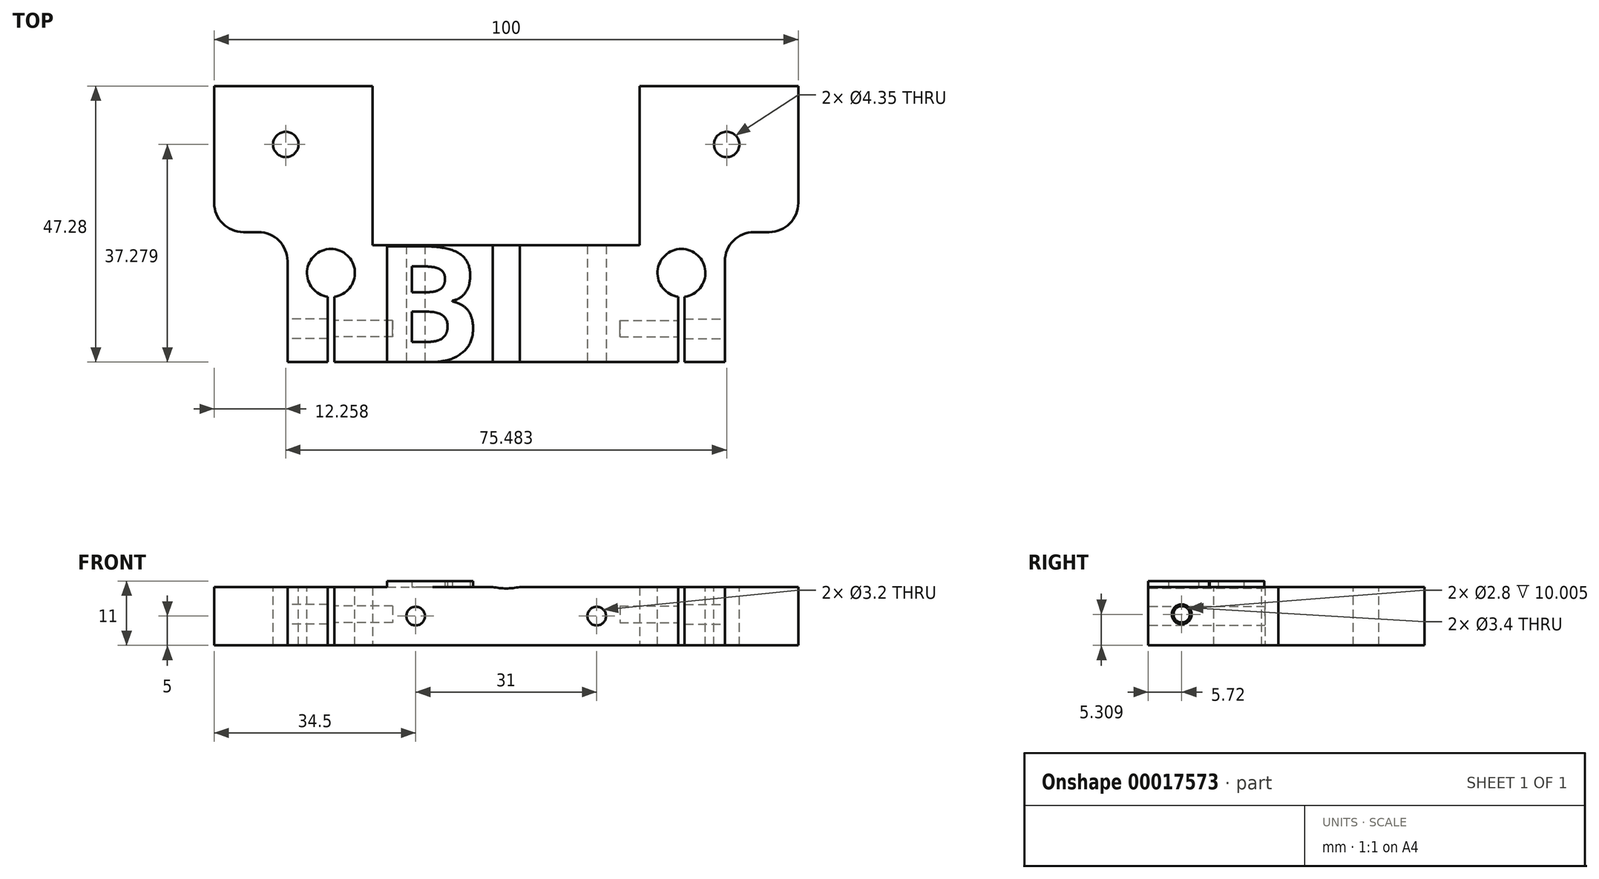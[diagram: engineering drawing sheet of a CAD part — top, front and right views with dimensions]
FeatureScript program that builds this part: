
annotation { "Feature Type Name" : "Feature", "Feature Type Description" : "" }
export const myFeature = defineFeature(function(context is Context, id is Id, definition is map)
    precondition{}
    {
        {
            var Q0;
            Q0=qCreatedBy(makeId("Top.planeOp"),FACE);
            var sketch = newSketch(context, id + "F0", { "sketchPlane" : qUnion([Q0])});
            skLineSegment(sketch, "E0", {"start": v(0, -13.82) * mm, "end": v(-37.44, -13.82) * mm});
            skLineSegment(sketch, "E1", {"start": v(-37.44, -13.82) * mm, "end": v(-37.44, 8.46) * mm});
            skLineSegment(sketch, "E2", {"start": v(-37.44, 8.46) * mm, "end": v(-50, 8.46) * mm});
            skLineSegment(sketch, "E3", {"start": v(-50, 8.46) * mm, "end": v(-50, 33.46) * mm});
            skLineSegment(sketch, "E4", {"start": v(-50, 33.46) * mm, "end": v(-22.87, 33.46) * mm});
            skLineSegment(sketch, "E5", {"start": v(-22.87, 33.46) * mm, "end": v(-22.87, 6.18) * mm});
            skLineSegment(sketch, "E6", {"start": v(-22.87, 6.18) * mm, "end": v(0, 6.18) * mm});
            skLineSegment(sketch, "E7", {"start": v(0, 6.18) * mm, "end": v(0, -13.82) * mm});
            skSolve(sketch);
        }
        {
            var Q0;
            Q0=qSketchRegion(id+"F0",true);
            extrude(context, id + "F1", {"entities" : qUnion([Q0]), "depth" : 10 * mm});
        }
        {
            var Q0;
            Q0=makeQuery(id+"F1.opExtrude","SWEPT_FACE",FACE,{"disambiguationData":[OSD([sQuery(id+"F0.wireOp",EDGE,"E0")])]});
            var sketch = newSketch(context, id + "F2", { "sketchPlane" : qUnion([Q0])});
            skLineSegment(sketch, "E8", {"start": v(0, 5) * mm, "end": v(0, 5) * mm});
            skCircle(sketch, "E9", {"center": v(-15.5, 5) * mm, "radius": 1.6 * mm});
            skCircle(sketch, "E10", {"center": v(0, 20.5) * mm, "radius": 10.75 * mm});
            skSolve(sketch);
        }
        {
            var Q0;
            Q0=qSketchRegion(id+"F2",true);
            extrude(context, id + "F3", {"entities" : qUnion([Q0]), "operationType" : NewBodyOperationType.REMOVE, "endBound" : BoundingType.THROUGH_ALL, "oppositeDirection" : true, "depth" : 25 * mm});
        }
        {
            var Q0;
            {var subQ0=makeQuery(id+"F1.opExtrude","CAP_FACE",FACE,{"disambiguationData":[OSD([sQuery(id+"F0.wireOp",EDGE,"E0"),sQuery(id+"F0.wireOp",EDGE,"fd64a43a-5635-4f94-a977-4dd36923accb"),sQuery(id+"F0.wireOp",EDGE,"1334f7d4-4c90-4769-8fa3-fe5f576fb005"),sQuery(id+"F0.wireOp",EDGE,"E1"),sQuery(id+"F0.wireOp",EDGE,"E2"),sQuery(id+"F0.wireOp",EDGE,"E3"),sQuery(id+"F0.wireOp",EDGE,"E4"),sQuery(id+"F0.wireOp",EDGE,"E5"),sQuery(id+"F0.wireOp",EDGE,"E6"),sQuery(id+"F0.wireOp",EDGE,"E7")])],"isStart":false});Q0=makeQuery(id+"F11.boolean.opBoolean","MERGE",FACE,{"derivedFrom":[subQ0,makeQuery(id+"F11.opPattern","COPY",FACE,{"derivedFrom":subQ0,"instanceName":"1"})]});}
            var sketch = newSketch(context, id + "F4", { "sketchPlane" : qUnion([Q0])});
            skCircle(sketch, "E11", {"center": v(-30, 1.46) * mm, "radius": 4.1 * mm});
            skCircle(sketch, "E12", {"center": v(-37.74, 23.46) * mm, "radius": 2.17 * mm});
            skLineSegment(sketch, "E13", {"start": v(-30, 1.46) * mm, "end": v(-30, -13.82) * mm, "construction": true});
            skLineSegment(sketch, "E14.bottom", {"start": v(-30.55, -1.63) * mm, "end": v(-29.45, -1.63) * mm});
            skLineSegment(sketch, "E14.top", {"start": v(-30.55, -14.74) * mm, "end": v(-29.45, -14.74) * mm});
            skLineSegment(sketch, "E14.left", {"start": v(-30.55, -1.63) * mm, "end": v(-30.55, -14.74) * mm});
            skLineSegment(sketch, "E14.right", {"start": v(-29.45, -1.63) * mm, "end": v(-29.45, -14.74) * mm});
            skPoint(sketch, "E15", {"position": v(-30, -1.63) * mm});
            skSolve(sketch);
        }
        {
            var Q0;
            Q0=qSketchRegion(id+"F4",true);
            var Q1;
            {var subQ3=sQuery(id+"F4.wireOp",EDGE,"E14.bottom");Q1=makeQuery(id+"F4.imprint","IMPRINT",FACE,{"disambiguationData":[TD([[makeQuery(id+"F4.imprint","IMPRINT",EDGE,{"derivedFrom":subQ3}),-1.0]])]});}
            extrude(context, id + "F5", {"entities" : qUnion([Q0, Q1]), "operationType" : NewBodyOperationType.REMOVE, "endBound" : BoundingType.THROUGH_ALL, "oppositeDirection" : true, "depth" : 25 * mm});
        }
        {
            var Q0;
            Q0=makeQuery(id+"F1.opExtrude","SWEPT_EDGE",EDGE,{"disambiguationData":[OSD([sQuery(id+"F0.wireOp",EDGE,"E2"),sQuery(id+"F0.wireOp",EDGE,"E3")])]});
            fillet(context, id + "F6", {"entities" : qUnion([Q0]), "radius" : 5 * mm, "tangentPropagation" : true, "allowEdgeOverflow" : false});
        }
        {
            var Q0;
            Q0=makeQuery(id+"F1.opExtrude","SWEPT_EDGE",EDGE,{"disambiguationData":[OSD([sQuery(id+"F0.wireOp",EDGE,"E1"),sQuery(id+"F0.wireOp",EDGE,"E2")])]});
            fillet(context, id + "F7", {"entities" : qUnion([Q0]), "radius" : 5 * mm, "tangentPropagation" : true, "allowEdgeOverflow" : false});
        }
        {
            var Q0;
            Q0=makeQuery(id+"F1.opExtrude","SWEPT_FACE",FACE,{"disambiguationData":[OSD([sQuery(id+"F0.wireOp",EDGE,"E1")])]});
            var sketch = newSketch(context, id + "F8", { "sketchPlane" : qUnion([Q0])});
            skCircle(sketch, "E16", {"center": v(8.1, 5.3) * mm, "radius": 1.7 * mm});
            skCircle(sketch, "E17", {"center": v(8.1, 5.3) * mm, "radius": 1.4 * mm});
            skSolve(sketch);
        }
        {
            var Q0;
            Q0=makeQuery(id+"F8.imprint","IMPRINT",FACE,{"disambiguationData":[TD([[makeQuery(id+"F8.imprint","IMPRINT",EDGE,{"derivedFrom":sQuery(id+"F8.wireOp",EDGE,"E17")}),1.0]])]});
            extrude(context, id + "F9", {"entities" : qUnion([Q0]), "operationType" : NewBodyOperationType.REMOVE, "oppositeDirection" : true, "depth" : 18 * mm});
        }
        {
            var Q0;
            Q0=makeQuery(id+"F8.imprint","IMPRINT",FACE,{"disambiguationData":[TD([[makeQuery(id+"F8.imprint","IMPRINT",EDGE,{"derivedFrom":sQuery(id+"F8.wireOp",EDGE,"E17")}),1.0]])]});
            var Q1;
            Q1=makeQuery(id+"F8.imprint","IMPRINT",FACE,{"disambiguationData":[TD([[makeQuery(id+"F8.imprint","IMPRINT",EDGE,{"derivedFrom":sQuery(id+"F8.wireOp",EDGE,"E16")}),1.0]])]});
            extrude(context, id + "F10", {"entities" : qUnion([Q0, Q1]), "operationType" : NewBodyOperationType.REMOVE, "endBound" : BoundingType.UP_TO_NEXT, "oppositeDirection" : true, "depth" : 25 * mm});
        }
        {
            var Q0;
            Q0=makeQuery(id+"F1.opExtrude","SWEPT_BODY",BODY,{"disambiguationData":[OSD([sQuery(id+"F0.wireOp",EDGE,"E0"),sQuery(id+"F0.wireOp",EDGE,"fd64a43a-5635-4f94-a977-4dd36923accb"),sQuery(id+"F0.wireOp",EDGE,"1334f7d4-4c90-4769-8fa3-fe5f576fb005"),sQuery(id+"F0.wireOp",EDGE,"E1"),sQuery(id+"F0.wireOp",EDGE,"E2"),sQuery(id+"F0.wireOp",EDGE,"E3"),sQuery(id+"F0.wireOp",EDGE,"E4"),sQuery(id+"F0.wireOp",EDGE,"E5"),sQuery(id+"F0.wireOp",EDGE,"E6"),sQuery(id+"F0.wireOp",EDGE,"E7")])]});
            var Q1;
            Q1=qCreatedBy(makeId("Right.planeOp"),FACE);
            mirror(context, id + "F11", {"operationType" : NewBodyOperationType.ADD, "entities" : qUnion([Q0]), "mirrorPlane" : qUnion([Q1])});
        }
        {
            var Q0;
            Q0=makeQuery(id+"F1.opExtrude","CAP_FACE",FACE,{"disambiguationData":[OSD([sQuery(id+"F0.wireOp",EDGE,"E0"),sQuery(id+"F0.wireOp",EDGE,"E1"),sQuery(id+"F0.wireOp",EDGE,"E2"),sQuery(id+"F0.wireOp",EDGE,"E3"),sQuery(id+"F0.wireOp",EDGE,"E4"),sQuery(id+"F0.wireOp",EDGE,"E5"),sQuery(id+"F0.wireOp",EDGE,"E6"),sQuery(id+"F0.wireOp",EDGE,"E7")])],"isStart":false});
            var sketch = newSketch(context, id + "F12", { "sketchPlane" : qUnion([Q0])});
            skText(sketch, "E18", { "text": "B", "fontName": "OpenSans-Bold.ttf"});
            const initialGuessF12  = {"E18": [-0.02287, -0.01382, 1, 0, 0.02]};
            skSetInitialGuess(sketch, initialGuessF12);
            skSolve(sketch);
        }
        {
            var Q0;
            Q0=qSketchRegion(id+"F12",true);
            extrude(context, id + "F13", {"entities" : qUnion([Q0]), "operationType" : NewBodyOperationType.ADD, "depth" : 1 * mm});
        }
    });
